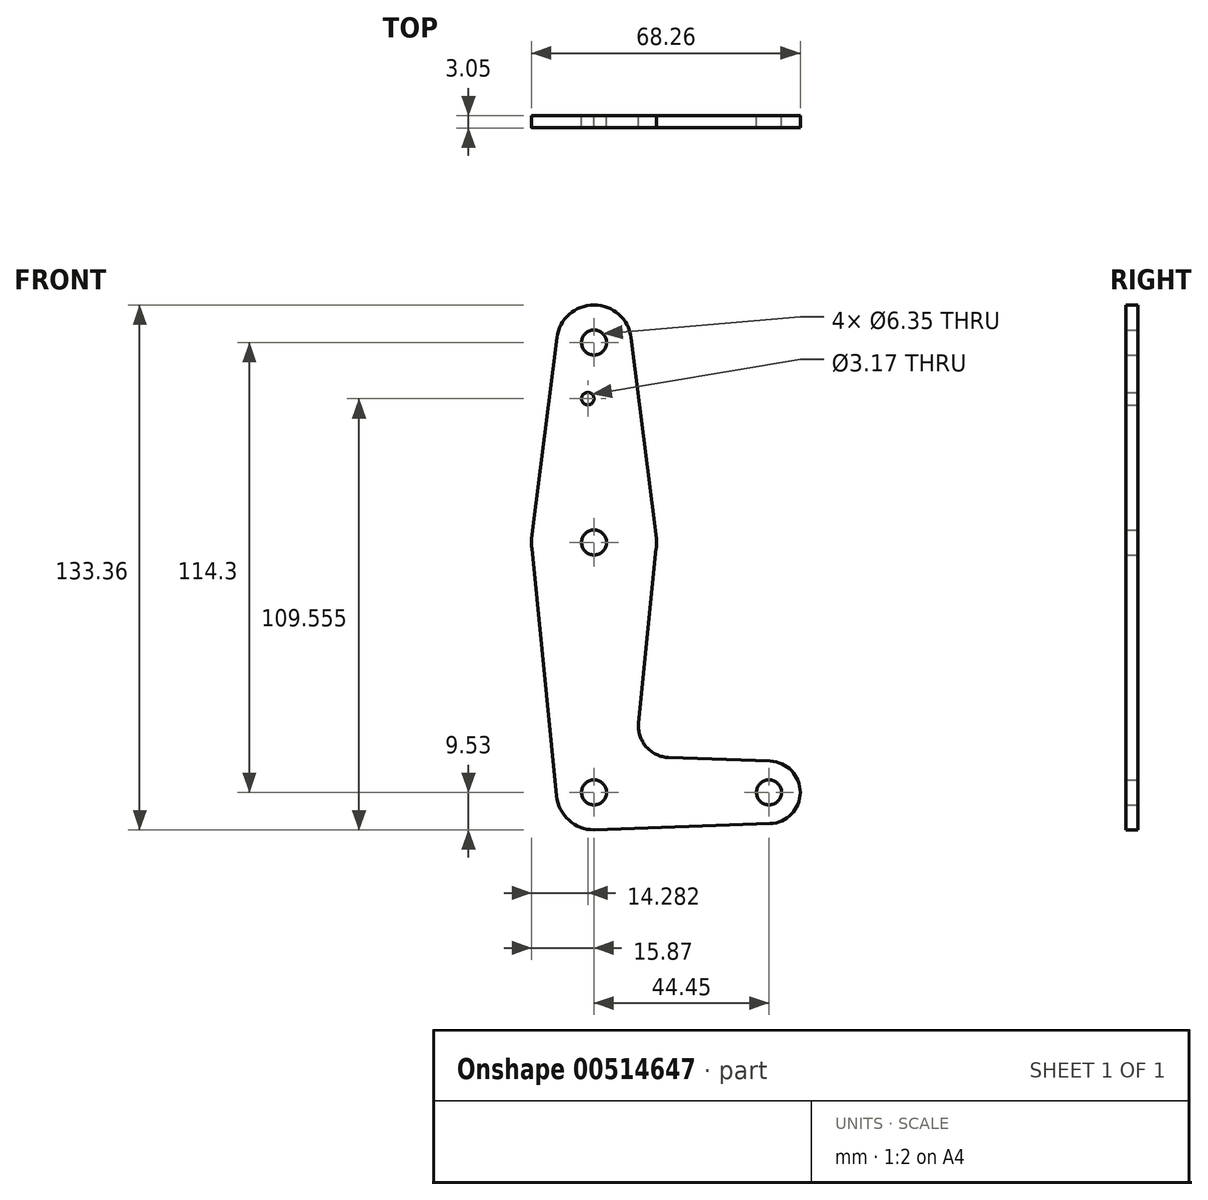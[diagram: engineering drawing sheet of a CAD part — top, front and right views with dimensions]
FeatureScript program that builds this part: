
annotation { "Feature Type Name" : "Feature", "Feature Type Description" : "" }
export const myFeature = defineFeature(function(context is Context, id is Id, definition is map)
    precondition{}
    {
        {
            var Q0;
            Q0=qCreatedBy(makeId("Front.planeOp"),FACE);
            var sketch = newSketch(context, id + "F0", { "sketchPlane" : qUnion([Q0])});
            skLineSegment(sketch, "E0", {"start": v(0, 0) * mm, "end": v(0, 114.3) * mm, "construction": true});
            skLineSegment(sketch, "E1", {"start": v(0, 0) * mm, "end": v(44.45, 0) * mm, "construction": true});
            skCircle(sketch, "E2", {"center": v(0, 114.3) * mm, "radius": 9.53 * mm});
            skCircle(sketch, "E3", {"center": v(44.45, 0) * mm, "radius": 7.94 * mm});
            skCircle(sketch, "E4", {"center": v(0, 0) * mm, "radius": 9.53 * mm});
            skCircle(sketch, "E5", {"center": v(0, 63.5) * mm, "radius": 15.88 * mm});
            skLineSegment(sketch, "E6", {"start": v(9.45, 115.5) * mm, "end": v(15.75, 65.48) * mm});
            skLineSegment(sketch, "E7", {"start": v(-15.8, 61.91) * mm, "end": v(-9.48, -0.95) * mm});
            skLineSegment(sketch, "E8", {"start": v(15.8, 61.91) * mm, "end": v(11.34, 17.6) * mm});
            skLineSegment(sketch, "E9", {"start": v(18.97, 8.85) * mm, "end": v(44.73, 7.93) * mm});
            skLineSegment(sketch, "E10", {"start": v(0, -9.53) * mm, "end": v(44.73, -7.93) * mm});
            skLineSegment(sketch, "E11", {"start": v(-9.45, 115.5) * mm, "end": v(-15.75, 65.48) * mm});
            skCircle(sketch, "E12", {"center": v(0, 114.3) * mm, "radius": 3.18 * mm});
            skCircle(sketch, "E13", {"center": v(0, 63.5) * mm, "radius": 3.18 * mm});
            skCircle(sketch, "E14", {"center": v(0, 0) * mm, "radius": 3.18 * mm});
            skCircle(sketch, "E15", {"center": v(44.45, 0) * mm, "radius": 3.18 * mm});
            skCircle(sketch, "E16", {"center": v(-1.59, 100.03) * mm, "radius": 1.59 * mm});
            skArc(sketch, "E17.filletArc", {"start": v(11.34, 17.6) * mm, "mid": v(13.26, 11.57) * mm, "end": v(18.97, 8.85) * mm});
            skSolve(sketch);
        }
        {
            var Q0;
            Q0=makeQuery(id+"F0.imprint","IMPRINT",FACE,{"disambiguationData":[TD([[makeQuery(id+"F0.imprint","IMPRINT",EDGE,{"derivedFrom":sQuery(id+"F0.wireOp",EDGE,"E12")}),-1.0]])]});
            var Q1;
            {var subQ1=sQuery(id+"F0.wireOp",EDGE,"E6");Q1=makeQuery(id+"F0.imprint","IMPRINT",FACE,{"disambiguationData":[TD([[makeQuery(id+"F0.imprint","IMPRINT",EDGE,{"derivedFrom":subQ1}),-1.0]])]});}
            var Q2;
            Q2=makeQuery(id+"F0.imprint","IMPRINT",FACE,{"disambiguationData":[TD([[makeQuery(id+"F0.imprint","IMPRINT",EDGE,{"derivedFrom":sQuery(id+"F0.wireOp",EDGE,"E13")}),-1.0]])]});
            var Q3;
            {var subQ0=sQuery(id+"F0.wireOp",EDGE,"E7");Q3=makeQuery(id+"F0.imprint","IMPRINT",FACE,{"disambiguationData":[TD([[makeQuery(id+"F0.imprint","IMPRINT",EDGE,{"derivedFrom":subQ0}),1.0]])]});}
            var Q4;
            Q4=makeQuery(id+"F0.imprint","IMPRINT",FACE,{"disambiguationData":[TD([[makeQuery(id+"F0.imprint","IMPRINT",EDGE,{"derivedFrom":sQuery(id+"F0.wireOp",EDGE,"E14")}),-1.0]])]});
            var Q5;
            Q5=makeQuery(id+"F0.imprint","IMPRINT",FACE,{"disambiguationData":[TD([[makeQuery(id+"F0.imprint","IMPRINT",EDGE,{"derivedFrom":sQuery(id+"F0.wireOp",EDGE,"E15")}),-1.0]])]});
            extrude(context, id + "F1", {"entities" : qUnion([Q0, Q1, Q2, Q3, Q4, Q5]), "depth" : 3.05 * mm, "offsetDistance" : 25.4 * mm});
        }
    });
